# Revit family: Shower-Shower_Door-KOHLER-Purist-K-705705
name_source: partatom
category: Generic Models
revit_build: Autodesk Revit 2015 (Build: 20140606_1530(x64)
units: mm (PartAtom-declared; Revit-internal decimal feet)

## types (3) — shared parameters
ADA = No
Assembly Code = D2010700
Cold Water Inlet = Cold Water Inlet
Date Modified = 01/30/2018
Default Elevation = 0"
Description = Pivot shower door, 72-1/4 inch H x 57-1/4 inch to 59 3/4 inch W, with 3/8 inch thick Crystal Clear glass
Height = 72 1/4"
Hot Water Inlet = Hot Water Inlet
Length = 57 1/4"
Manufacturer = KOHLER Co.
MasterFormat 1995 = 15410
MasterFormat 2004 = 22.41.23
Material = Anodized aluminum prevents rusting or corrosion and Tempered glass ensures maximum safety and durability
Panel Thickness = 0"
Product Documentation Link = http://www.us.kohler.com
Product Name = Purist
Product Page URL = http://www.us.kohler.com
URL = https://www.us.kohler.com
Waste Water Outlet = Waste Water Outlet
Width = 2 9/16"

## per-type parameters (varying)
| type | Finish | Model | Type |
| SHP-Bright Polished Silver | Kohler-Metal-SHP-Bright_Polished_Silver | K-705705-L-SHP | 1 |
| NX-Brushed Nickel | Kohler-Metal-NX-Brushed_Nickel | K-705705-L-NX | 2 |
| ABV-Anodized Brushed Bronze | Kohler-Metal-ABV-Anodized_Brushed_Bronze | K-705705-L-ABV | 3 |

## geometry (parser evidence)
native form markers: Sweep x17
no freeform markers — native parametric forms only
